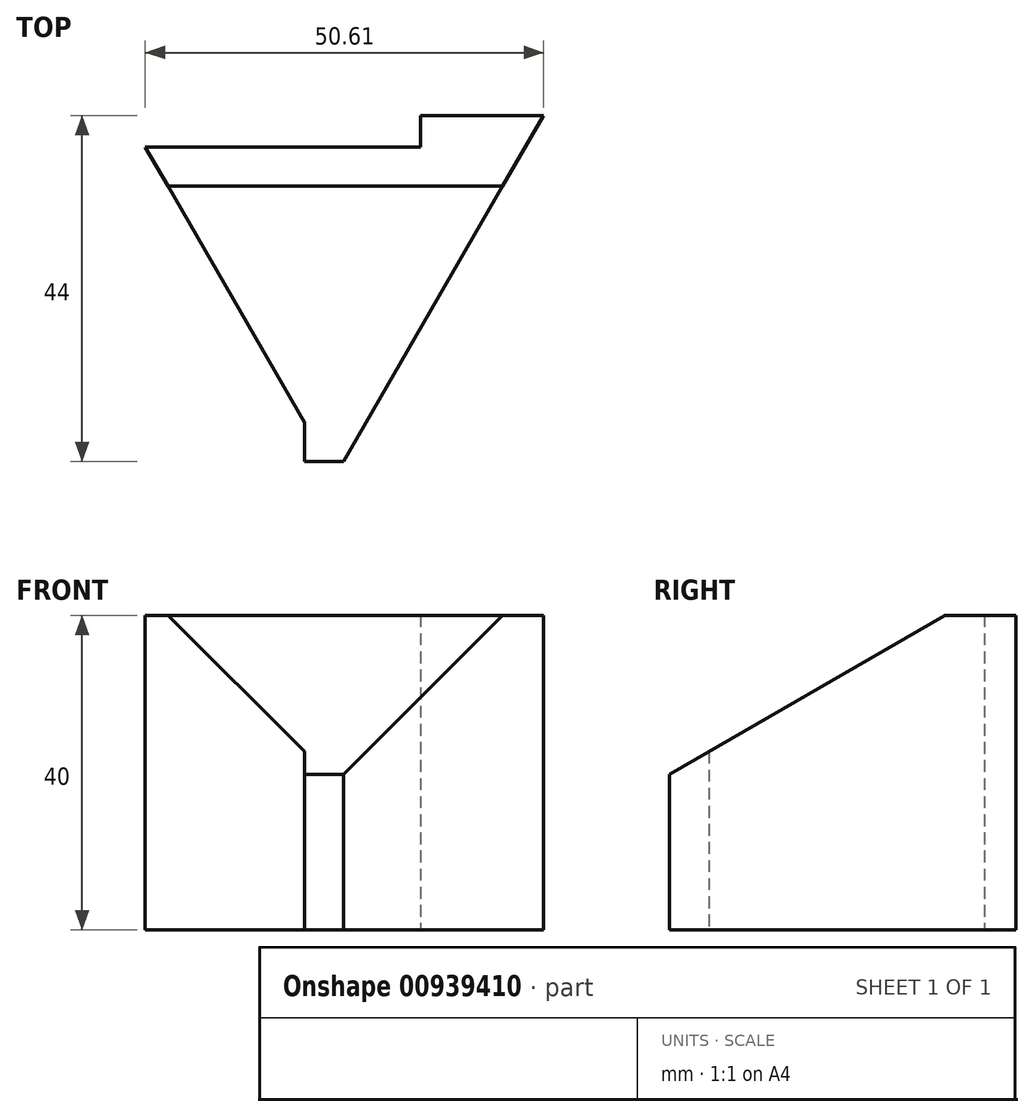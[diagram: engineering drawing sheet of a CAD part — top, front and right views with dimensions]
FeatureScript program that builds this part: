
annotation { "Feature Type Name" : "Feature", "Feature Type Description" : "" }
export const myFeature = defineFeature(function(context is Context, id is Id, definition is map)
    precondition{}
    {
        {
            var Q0;
            Q0=qCreatedBy(makeId("Top.planeOp"),FACE);
            var sketch = newSketch(context, id + "F0", { "sketchPlane" : qUnion([Q0])});
            skLineSegment(sketch, "E0", {"start": v(0, 0) * mm, "end": v(0, 40) * mm, "construction": true});
            skLineSegment(sketch, "E1", {"start": v(0, 0) * mm, "end": v(-5, 0) * mm});
            skLineSegment(sketch, "E2", {"start": v(-5, 0) * mm, "end": v(-5, 5) * mm});
            skLineSegment(sketch, "E3", {"start": v(-5, 5) * mm, "end": v(-25.2, 40) * mm});
            skLineSegment(sketch, "E4", {"start": v(-25.2, 40) * mm, "end": v(0, 40) * mm});
            skLineSegment(sketch, "E5", {"start": v(0, 0) * mm, "end": v(25.4, 44) * mm});
            skLineSegment(sketch, "E6", {"start": v(9.8, 40) * mm, "end": v(0, 40) * mm});
            skLineSegment(sketch, "E7", {"start": v(9.8, 40) * mm, "end": v(9.8, 44) * mm});
            skLineSegment(sketch, "E8", {"start": v(9.8, 44) * mm, "end": v(25.4, 44) * mm});
            skPoint(sketch, "E9.orphan", {"position": v(23.1, 40) * mm});
            skSolve(sketch);
        }
        {
            var Q0;
            Q0=makeQuery(id+"F0.imprint","IMPRINT",FACE,{"disambiguationData":[TD([[makeQuery(id+"F0.imprint","IMPRINT",EDGE,{"derivedFrom":sQuery(id+"F0.wireOp",EDGE,"E1")}),-1.0]])]});
            extrude(context, id + "F1", {"entities" : qUnion([Q0]), "depth" : 40 * mm, "offsetDistance" : 25 * mm});
        }
        {
            var Q0;
            Q0=qCreatedBy(makeId("Right.planeOp"),FACE);
            var sketch = newSketch(context, id + "F2", { "sketchPlane" : qUnion([Q0])});
            skLineSegment(sketch, "E10", {"start": v(0, 40) * mm, "end": v(35, 40) * mm});
            skLineSegment(sketch, "E11", {"start": v(35, 40) * mm, "end": v(0, 19.8) * mm});
            skLineSegment(sketch, "E12", {"start": v(0, 19.8) * mm, "end": v(0, 40) * mm});
            skSolve(sketch);
        }
        {
            var Q0;
            Q0 = qSketchRegion(id + "F2", true);
            extrude(context, id + "F3", {"entities" : qUnion([Q0]), "operationType" : NewBodyOperationType.REMOVE, "endBound" : BoundingType.THROUGH_ALL, "oppositeDirection" : true, "depth" : 25 * mm, "offsetDistance" : 25 * mm, "hasSecondDirection" : true, "secondDirectionOppositeDirection" : false, "secondDirectionDepth" : 25 * mm});
        }
    });
